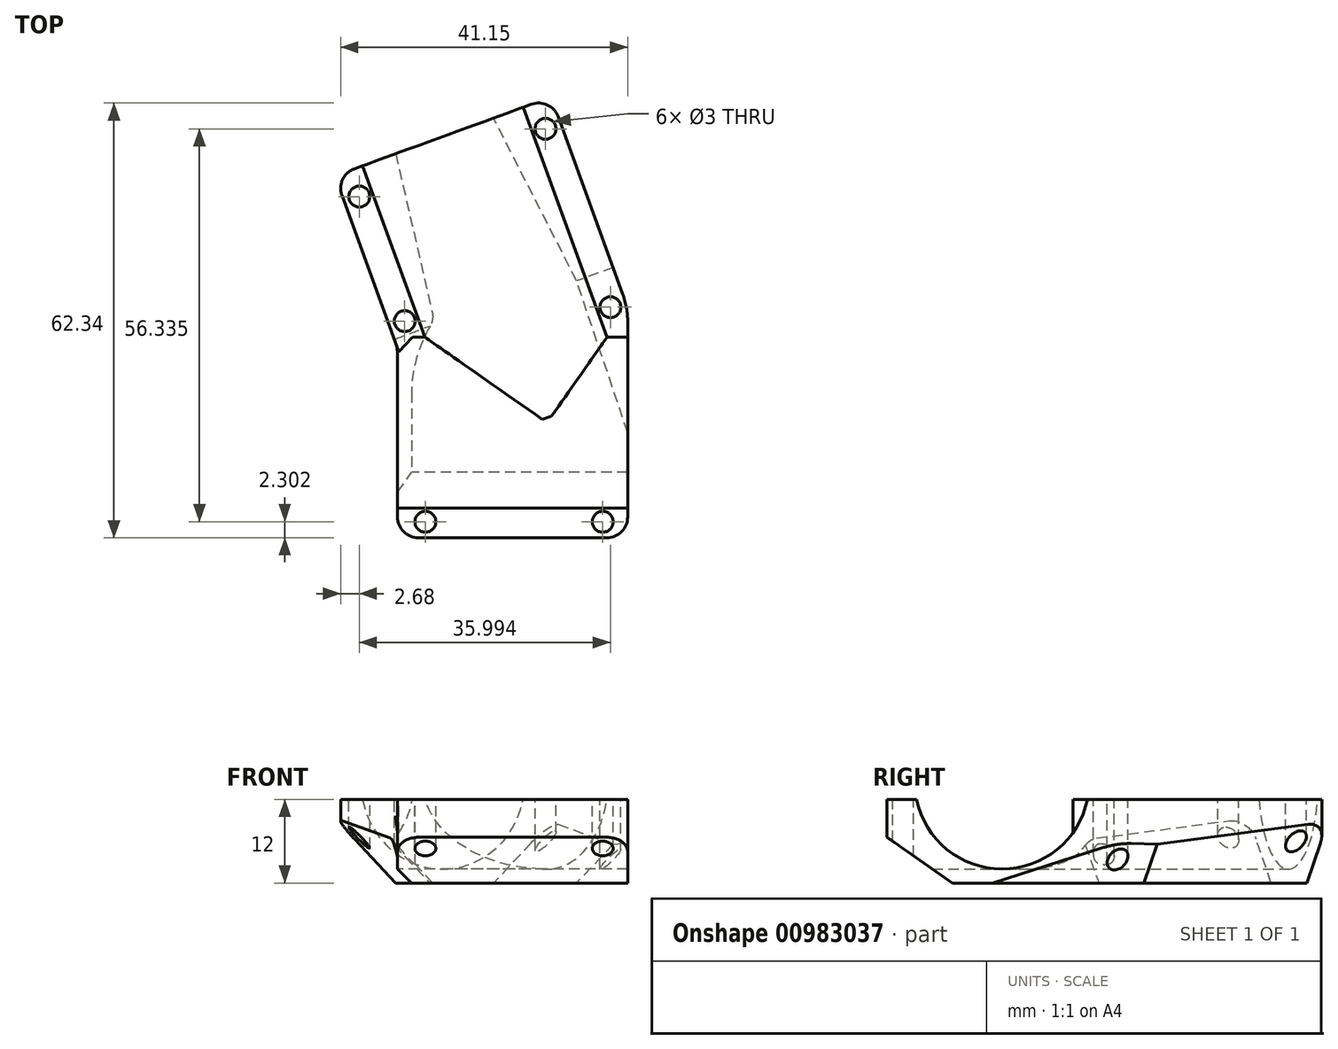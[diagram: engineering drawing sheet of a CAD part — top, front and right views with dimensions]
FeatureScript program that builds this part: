
annotation { "Feature Type Name" : "Feature", "Feature Type Description" : "" }
export const myFeature = defineFeature(function(context is Context, id is Id, definition is map)
    precondition{}
    {
        {
            var Q0;
            Q0=qCreatedBy(makeId("Top.planeOp"),FACE);
            var sketch = newSketch(context, id + "F0", { "sketchPlane" : qUnion([Q0])});
            skLineSegment(sketch, "E0.bottom", {"start": v(-31.25, 20.48) * mm, "end": v(1.75, 20.48) * mm});
            skLineSegment(sketch, "E0.top", {"start": v(-31.25, -12.52) * mm, "end": v(1.75, -12.52) * mm});
            skLineSegment(sketch, "E0.left", {"start": v(-31.25, 20.48) * mm, "end": v(-31.25, -12.52) * mm});
            skLineSegment(sketch, "E0.right", {"start": v(1.75, 20.48) * mm, "end": v(1.75, -12.52) * mm});
            skSolve(sketch);
        }
        {
            var Q0;
            Q0=qSketchRegion(id+"F0",true);
            extrude(context, id + "F1", {"entities" : qUnion([Q0]), "depth" : 12 * mm, "offsetDistance" : 25 * mm});
        }
        {
            var Q0;
            Q0=makeQuery(id+"F1.opExtrude","SWEPT_FACE",FACE,{"disambiguationData":[OSD([sQuery(id+"F0.wireOp",EDGE,"E0.left")])]});
            var sketch = newSketch(context, id + "F2", { "sketchPlane" : qUnion([Q0])});
            skCircle(sketch, "E1", {"center": v(-3.98, 14.5) * mm, "radius": 12.5 * mm});
            skPoint(sketch, "E1.centerSnap0", {"position": v(-3.98, 12) * mm});
            skSolve(sketch);
        }
        {
            var Q0;
            Q0=qSketchRegion(id+"F2",true);
            extrude(context, id + "F3", {"entities" : qUnion([Q0]), "operationType" : NewBodyOperationType.REMOVE, "oppositeDirection" : true, "depth" : 98.3 * mm, "offsetDistance" : 25 * mm});
        }
        {
            var Q0;
            {var subQ0=sQuery(id+"F0.wireOp",EDGE,"E0.top");var subQ1=sQuery(id+"F0.wireOp",EDGE,"E0.left");var subQ2=sQuery(id+"F0.wireOp",EDGE,"E0.right");Q0=makeQuery(id+"F3.boolean.opBoolean","SPLIT",FACE,{"disambiguationData":[TD([makeQuery(id+"F1.opExtrude","SWEPT_FACE",FACE,{"disambiguationData":[OSD([subQ0])]})])],"derivedFrom":makeQuery(id+"F1.opExtrude","CAP_FACE",FACE,{"disambiguationData":[OSD([sQuery(id+"F0.wireOp",EDGE,"E0.bottom"),subQ0,subQ1,subQ2])],"isStart":false})});}
            var sketch = newSketch(context, id + "F4", { "sketchPlane" : qUnion([Q0])});
            skLineSegment(sketch, "E2", {"start": v(1.75, -12.52) * mm, "end": v(-9.24, -42.7) * mm});
            skLineSegment(sketch, "E3.0", {"start": v(-33.37, -12.52) * mm, "end": v(-40.25, -31.41) * mm});
            skLineSegment(sketch, "E4", {"start": v(-40.25, -31.41) * mm, "end": v(-9.24, -42.7) * mm});
            skLineSegment(sketch, "E5", {"start": v(-33.37, -12.52) * mm, "end": v(-31.06, -6.17) * mm});
            skLineSegment(sketch, "E6", {"start": v(-31.06, -6.17) * mm, "end": v(-25.12, -12.52) * mm});
            skLineSegment(sketch, "E7", {"start": v(-25.12, -12.52) * mm, "end": v(1.75, -12.52) * mm});
            skSolve(sketch);
        }
        {
            var Q0;
            Q0=qSketchRegion(id+"F4",true);
            extrude(context, id + "F5", {"entities" : qUnion([Q0]), "operationType" : NewBodyOperationType.ADD, "oppositeDirection" : true, "depth" : 12 * mm, "offsetDistance" : 25 * mm});
        }
        {
            var Q0;
            Q0=makeQuery(id+"F5.opExtrude","SWEPT_FACE",FACE,{"disambiguationData":[OSD([sQuery(id+"F4.wireOp",EDGE,"E4")])]});
            var sketch = newSketch(context, id + "F6", { "sketchPlane" : qUnion([Q0])});
            skCircle(sketch, "E8", {"center": v(-10.58, 14.5) * mm, "radius": 12.5 * mm});
            skPoint(sketch, "E8.centerSnap0", {"position": v(-10.58, 12) * mm});
            skSolve(sketch);
        }
        {
            var Q0;
            Q0=qSketchRegion(id+"F6",true);
            extrude(context, id + "F7", {"entities" : qUnion([Q0]), "operationType" : NewBodyOperationType.REMOVE, "oppositeDirection" : true, "depth" : 43 * mm, "offsetDistance" : 25 * mm});
        }
        {
            var Q0;
            {var subQ0=sQuery(id+"F0.wireOp",EDGE,"E0.right");Q0=makeQuery(id+"F5.boolean.opBoolean","MERGE",EDGE,{"derivedFrom":[makeQuery(id+"F1.opExtrude","SWEPT_EDGE",EDGE,{"disambiguationData":[OSD([sQuery(id+"F0.wireOp",EDGE,"E0.top"),subQ0])]}),makeQuery(id+"F5.opExtrude","SWEPT_EDGE",EDGE,{"disambiguationData":[OSD([subQ0,sQuery(id+"F4.wireOp",EDGE,"E2"),sQuery(id+"F4.wireOp",EDGE,"E7")])]})]});}
            fillet(context, id + "F8", {"entities" : qUnion([Q0]), "radius" : 12 * mm, "tangentPropagation" : true, "allowEdgeOverflow" : false});
        }
        {
            var Q0;
            Q0=makeQuery(id+"F5.boolean.opBoolean","INTERSECT",EDGE,{"derivedFrom":[makeQuery(id+"F1.opExtrude","SWEPT_FACE",FACE,{"disambiguationData":[OSD([sQuery(id+"F0.wireOp",EDGE,"E0.left")])]}),makeQuery(id+"F5.opExtrude","SWEPT_FACE",FACE,{"disambiguationData":[OSD([sQuery(id+"F4.wireOp",EDGE,"E3.0"),sQuery(id+"F4.wireOp",EDGE,"E5")])]})]});
            fillet(context, id + "F9", {"entities" : qUnion([Q0]), "radius" : 5 * mm, "tangentPropagation" : true, "allowEdgeOverflow" : false});
        }
        {
            var Q0;
            {var subQ0=sQuery(id+"F4.wireOp",EDGE,"E4");var subQ1=sQuery(id+"F4.wireOp",EDGE,"E2");var subQ3=sQuery(id+"F0.wireOp",EDGE,"E0.right");var subQ4=makeQuery(id+"F1.opExtrude","SWEPT_FACE",FACE,{"disambiguationData":[OSD([subQ3])]});var subQ5=sQuery(id+"F0.wireOp",EDGE,"E0.top");var subQ6=sQuery(id+"F0.wireOp",EDGE,"E0.left");Q0=makeQuery(id+"F7.boolean.opBoolean","SPLIT",FACE,{"disambiguationData":[TD([subQ4])],"derivedFrom":makeQuery(id+"F5.boolean.opBoolean","MERGE",FACE,{"derivedFrom":[makeQuery(id+"F3.boolean.opBoolean","SPLIT",FACE,{"disambiguationData":[TD([makeQuery(id+"F1.opExtrude","SWEPT_FACE",FACE,{"disambiguationData":[OSD([subQ5])]})])],"derivedFrom":makeQuery(id+"F1.opExtrude","CAP_FACE",FACE,{"disambiguationData":[OSD([sQuery(id+"F0.wireOp",EDGE,"E0.bottom"),subQ5,subQ6,subQ3])],"isStart":false})}),makeQuery(id+"F5.opExtrude","CAP_FACE",FACE,{"disambiguationData":[OSD([subQ1,sQuery(id+"F4.wireOp",EDGE,"E3.0"),subQ0,sQuery(id+"F4.wireOp",EDGE,"E5"),sQuery(id+"F4.wireOp",EDGE,"E6"),sQuery(id+"F4.wireOp",EDGE,"E7")])],"isStart":true})]})});}
            var sketch = newSketch(context, id + "F10", { "sketchPlane" : qUnion([Q0])});
            skCircle(sketch, "E9", {"center": v(-36.72, -28.44) * mm, "radius": 1.5 * mm});
            skCircle(sketch, "E10", {"center": v(-10.03, -38.15) * mm, "radius": 1.5 * mm});
            skCircle(sketch, "E11", {"center": v(-30.22, -10.59) * mm, "radius": 1.5 * mm});
            skCircle(sketch, "E12", {"center": v(-0.73, -12.59) * mm, "radius": 1.5 * mm});
            skCircle(sketch, "E13", {"center": v(-1.83, 18.18) * mm, "radius": 1.5 * mm});
            skCircle(sketch, "E14", {"center": v(-27.25, 18.18) * mm, "radius": 1.5 * mm});
            skSolve(sketch);
        }
        {
            var Q0;
            Q0=qSketchRegion(id+"F10",true);
            extrude(context, id + "F11", {"entities" : qUnion([Q0]), "operationType" : NewBodyOperationType.REMOVE, "oppositeDirection" : true, "depth" : 25 * mm, "offsetDistance" : 25 * mm});
        }
        {
            var Q0;
            Q0=makeQuery(id+"F1.opExtrude","SWEPT_EDGE",EDGE,{"disambiguationData":[OSD([sQuery(id+"F0.wireOp",EDGE,"E0.bottom"),sQuery(id+"F0.wireOp",EDGE,"E0.left")])]});
            var Q1;
            Q1=makeQuery(id+"F5.opExtrude","SWEPT_EDGE",EDGE,{"disambiguationData":[OSD([sQuery(id+"F4.wireOp",EDGE,"E3.0"),sQuery(id+"F4.wireOp",EDGE,"E4")])]});
            var Q2;
            Q2=makeQuery(id+"F5.opExtrude","SWEPT_EDGE",EDGE,{"disambiguationData":[OSD([sQuery(id+"F4.wireOp",EDGE,"E2"),sQuery(id+"F4.wireOp",EDGE,"E4")])]});
            var Q3;
            Q3=makeQuery(id+"F1.opExtrude","SWEPT_EDGE",EDGE,{"disambiguationData":[OSD([sQuery(id+"F0.wireOp",EDGE,"E0.bottom"),sQuery(id+"F0.wireOp",EDGE,"E0.right")])]});
            fillet(context, id + "F12", {"entities" : qUnion([Q0, Q1, Q2, Q3]), "radius" : 3 * mm, "tangentPropagation" : true, "allowEdgeOverflow" : false});
        }
        {
            var Q0;
            Q0=makeQuery(id+"F5.opExtrude","SWEPT_FACE",FACE,{"disambiguationData":[OSD([sQuery(id+"F4.wireOp",EDGE,"E4")])]});
            var sketch = newSketch(context, id + "F13", { "sketchPlane" : qUnion([Q0])});
            skLineSegment(sketch, "E15", {"start": v(8.48, 11.34) * mm, "end": v(-5.11, -2.26) * mm});
            skLineSegment(sketch, "E16", {"start": v(-5.98, -11.8) * mm, "end": v(-35.58, 17.8) * mm});
            skLineSegment(sketch, "E17", {"start": v(-5.98, -11.8) * mm, "end": v(-40.13, -13.26) * mm});
            skLineSegment(sketch, "E18", {"start": v(-40.13, -13.26) * mm, "end": v(-35.6, 17.8) * mm});
            skLineSegment(sketch, "E19", {"start": v(-35.6, 17.8) * mm, "end": v(-35.58, 17.8) * mm});
            skLineSegment(sketch, "E20", {"start": v(8.48, 11.34) * mm, "end": v(10.35, -7.2) * mm});
            skLineSegment(sketch, "E21", {"start": v(10.35, -7.2) * mm, "end": v(-5.11, -2.26) * mm});
            skSolve(sketch);
        }
        {
            var Q0;
            Q0=qSketchRegion(id+"F13",true);
            extrude(context, id + "F14", {"entities" : qUnion([Q0]), "operationType" : NewBodyOperationType.REMOVE, "oppositeDirection" : true, "depth" : 26 * mm, "offsetDistance" : 25 * mm, "hasDraft" : true, "draftAngle" : 5 * degree, "draftPullDirection" : true});
        }
        {
            var Q0;
            Q0=makeQuery(id+"F14.boolean.opBoolean","COPY",FACE,{"derivedFrom":makeQuery(id+"F14.opExtrude","CAP_FACE",FACE,{"disambiguationData":[OSD([sQuery(id+"F13.wireOp",EDGE,"E15"),sQuery(id+"F13.wireOp",EDGE,"E20"),sQuery(id+"F13.wireOp",EDGE,"E21")])],"isStart":false})});
            var sketch = newSketch(context, id + "F15", { "sketchPlane" : qUnion([Q0])});
            skLineSegment(sketch, "E22.0", {"start": v(0.36, 0) * mm, "end": v(5.92, 0) * mm});
            skLineSegment(sketch, "E22.1", {"start": v(5.92, 5.56) * mm, "end": v(0.36, 0) * mm});
            skLineSegment(sketch, "E22.2", {"start": v(5.92, 0) * mm, "end": v(5.92, 5.56) * mm});
            skSolve(sketch);
        }
        {
            var Q0;
            Q0=qSketchRegion(id+"F15",true);
            extrude(context, id + "F16", {"entities" : qUnion([Q0]), "operationType" : NewBodyOperationType.REMOVE, "oppositeDirection" : true, "depth" : 25 * mm, "offsetDistance" : 25 * mm, "hasDraft" : true, "draftAngle" : 1 * degree});
        }
        {
            var Q0;
            Q0=makeQuery(id+"F14.boolean.opBoolean","COPY",EDGE,{"derivedFrom":makeQuery(id+"F14.opExtrude","CAP_EDGE",EDGE,{"disambiguationData":[OSD([sQuery(id+"F13.wireOp",EDGE,"E16")])],"isStart":false})});
            fillet(context, id + "F17", {"entities" : qUnion([Q0]), "radius" : 3 * mm, "tangentPropagation" : true, "allowEdgeOverflow" : false});
        }
        {
            var Q0;
            Q0=makeQuery(id+"F1.opExtrude","SWEPT_FACE",FACE,{"disambiguationData":[OSD([sQuery(id+"F0.wireOp",EDGE,"E0.left")])]});
            var sketch = newSketch(context, id + "F18", { "sketchPlane" : qUnion([Q0])});
            skLineSegment(sketch, "E23", {"start": v(-28.79, 12.38) * mm, "end": v(0, -7.78) * mm});
            skLineSegment(sketch, "E24", {"start": v(-1.67, -6.61) * mm, "end": v(-44.5, -59.45) * mm});
            skLineSegment(sketch, "E25", {"start": v(-44.5, -59.45) * mm, "end": v(-106.82, -49.14) * mm});
            skLineSegment(sketch, "E26", {"start": v(-106.82, -49.14) * mm, "end": v(-40.24, 11.89) * mm});
            skLineSegment(sketch, "E27", {"start": v(-40.24, 11.89) * mm, "end": v(-28.79, 12.38) * mm});
            skSolve(sketch);
        }
        {
            var Q0;
            Q0=qSketchRegion(id+"F18",true);
            extrude(context, id + "F19", {"entities" : qUnion([Q0]), "operationType" : NewBodyOperationType.REMOVE, "oppositeDirection" : true, "depth" : 38.9 * mm, "offsetDistance" : 25 * mm});
        }
        {
            var Q0;
            Q0=makeQuery(id+"F1.opExtrude","CAP_EDGE",EDGE,{"disambiguationData":[OSD([sQuery(id+"F0.wireOp",EDGE,"E0.left")])],"isStart":true});
            chamfer(context, id + "F20", {"entities" : qUnion([Q0]), "width" : 2 * mm, "tangentPropagation" : true});
        }
        {
            var Q0;
            {var subQ0=sQuery(id+"F4.wireOp",EDGE,"E5");var subQ1=sQuery(id+"F4.wireOp",EDGE,"E3.0");var subQ2=sQuery(id+"F0.wireOp",EDGE,"E0.left");Q0=makeQuery(id+"F20.opChamfer","BLEND_EDGE",EDGE,{"blendedFrom":[makeQuery(id+"F9.opFillet","BLEND_EDGE",EDGE,{"blendedFrom":[makeQuery(id+"F5.boolean.opBoolean","INTERSECT",EDGE,{"derivedFrom":[makeQuery(id+"F1.opExtrude","SWEPT_FACE",FACE,{"disambiguationData":[OSD([subQ2])]}),makeQuery(id+"F5.opExtrude","SWEPT_FACE",FACE,{"disambiguationData":[OSD([subQ1,subQ0])]})]}),makeQuery(id+"F5.boolean.opBoolean","MERGE",FACE,{"derivedFrom":[makeQuery(id+"F1.opExtrude","CAP_FACE",FACE,{"disambiguationData":[OSD([sQuery(id+"F0.wireOp",EDGE,"E0.bottom"),sQuery(id+"F0.wireOp",EDGE,"E0.top"),subQ2,sQuery(id+"F0.wireOp",EDGE,"E0.right")])],"isStart":true}),makeQuery(id+"F5.opExtrude","CAP_FACE",FACE,{"disambiguationData":[OSD([sQuery(id+"F4.wireOp",EDGE,"E2"),subQ1,sQuery(id+"F4.wireOp",EDGE,"E4"),subQ0,sQuery(id+"F4.wireOp",EDGE,"E6"),sQuery(id+"F4.wireOp",EDGE,"E7")])],"isStart":false})]})],"blendedInto":[makeQuery(id+"F5.boolean.opBoolean","MERGE",FACE,{"derivedFrom":[makeQuery(id+"F1.opExtrude","CAP_FACE",FACE,{"disambiguationData":[OSD([sQuery(id+"F0.wireOp",EDGE,"E0.bottom"),sQuery(id+"F0.wireOp",EDGE,"E0.top"),subQ2,sQuery(id+"F0.wireOp",EDGE,"E0.right")])],"isStart":true}),makeQuery(id+"F5.opExtrude","CAP_FACE",FACE,{"disambiguationData":[OSD([sQuery(id+"F4.wireOp",EDGE,"E2"),subQ1,sQuery(id+"F4.wireOp",EDGE,"E4"),subQ0,sQuery(id+"F4.wireOp",EDGE,"E6"),sQuery(id+"F4.wireOp",EDGE,"E7")])],"isStart":false})]})]}),makeQuery(id+"F14.boolean.opBoolean","COPY",FACE,{"derivedFrom":makeQuery(id+"F14.opExtrude","CAP_FACE",FACE,{"disambiguationData":[OSD([sQuery(id+"F13.wireOp",EDGE,"E16"),sQuery(id+"F13.wireOp",EDGE,"E17"),sQuery(id+"F13.wireOp",EDGE,"E18"),sQuery(id+"F13.wireOp",EDGE,"E19")])],"isStart":false})})],"blendedInto":[makeQuery(id+"F14.boolean.opBoolean","COPY",FACE,{"derivedFrom":makeQuery(id+"F14.opExtrude","CAP_FACE",FACE,{"disambiguationData":[OSD([sQuery(id+"F13.wireOp",EDGE,"E16"),sQuery(id+"F13.wireOp",EDGE,"E17"),sQuery(id+"F13.wireOp",EDGE,"E18"),sQuery(id+"F13.wireOp",EDGE,"E19")])],"isStart":false})})]});}
            fillet(context, id + "F21", {"entities" : qUnion([Q0]), "radius" : 20 * mm, "tangentPropagation" : true, "allowEdgeOverflow" : false});
        }
        {
            var Q0;
            Q0=makeQuery(id+"F1.opExtrude","SWEPT_BODY",BODY,{"disambiguationData":[OSD([sQuery(id+"F0.wireOp",EDGE,"E0.bottom"),sQuery(id+"F0.wireOp",EDGE,"E0.top"),sQuery(id+"F0.wireOp",EDGE,"E0.left"),sQuery(id+"F0.wireOp",EDGE,"E0.right")])]});
            var Q1;
            Q1=makeQuery(id+"F1.opExtrude","SWEPT_FACE",FACE,{"disambiguationData":[OSD([sQuery(id+"F0.wireOp",EDGE,"E0.bottom")])]});
            mirror(context, id + "F22", {"operationType" : NewBodyOperationType.ADD, "entities" : qUnion([Q0]), "mirrorPlane" : qUnion([Q1])});
        }
        {
            var Q0;
            {var subQ0=sQuery(id+"F0.wireOp",EDGE,"E0.bottom");var subQ1=sQuery(id+"F0.wireOp",EDGE,"E0.right");var subQ2=sQuery(id+"F0.wireOp",EDGE,"E0.left");var subQ3=makeQuery(id+"F3.boolean.opBoolean","SPLIT",FACE,{"disambiguationData":[TD([makeQuery(id+"F1.opExtrude","SWEPT_FACE",FACE,{"disambiguationData":[OSD([subQ0])]})])],"derivedFrom":makeQuery(id+"F1.opExtrude","CAP_FACE",FACE,{"disambiguationData":[OSD([subQ0,sQuery(id+"F0.wireOp",EDGE,"E0.top"),subQ2,subQ1])],"isStart":false})});Q0=makeQuery(id+"F22.boolean.opBoolean","MERGE",FACE,{"derivedFrom":[subQ3,makeQuery(id+"F22.opPattern","COPY",FACE,{"derivedFrom":subQ3,"instanceName":"1"})]});}
            var sketch = newSketch(context, id + "F23", { "sketchPlane" : qUnion([Q0])});
            skLineSegment(sketch, "E28.bottom", {"start": v(-52.23, 20.48) * mm, "end": v(10.9, 20.48) * mm});
            skLineSegment(sketch, "E28.top", {"start": v(-52.23, -54.72) * mm, "end": v(10.9, -54.72) * mm});
            skLineSegment(sketch, "E28.left", {"start": v(-52.23, 20.48) * mm, "end": v(-52.23, -54.72) * mm});
            skLineSegment(sketch, "E28.right", {"start": v(10.9, 20.48) * mm, "end": v(10.9, -54.72) * mm});
            skSolve(sketch);
        }
        {
            var Q0;
            Q0 = qSketchRegion(id + "F23", true);
            extrude(context, id + "F24", {"entities" : qUnion([Q0]), "operationType" : NewBodyOperationType.REMOVE, "oppositeDirection" : true, "depth" : 25 * mm, "offsetDistance" : 25 * mm});
        }
    });
